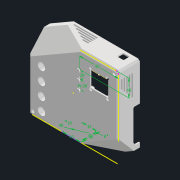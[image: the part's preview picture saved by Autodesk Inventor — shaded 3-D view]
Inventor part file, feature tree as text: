
AUTODESK INVENTOR PART (.ipt)
format: ipt  version: 2022 (Build 260153000, 153)  size: 850,944 bytes
history: native  units: mm
features: extrude x14, sketch x12, projected_geometry x9, fillet x8, other x8, chamfer x6, hole x5, reference x5, shell x1
ambient origin geometry x8: Origin, YZ Plane, XZ Plane, XY Plane, X Axis, Y Axis, Z Axis, Center Point
bodies: Solid1 (feature_tree)
feature tree (68):
  extrude  "Extrusion1"  Depth=2.0mm TaperAngle=45.0deg
  chamfer  "Chamfer1"  Distance=2.0mm Angle=45.0deg
  chamfer  "Chamfer2"  Distance=2.0mm Angle=45.0deg
  chamfer  "Chamfer3"  Distance=3.0mm
  shell  "Shell1"  Thickness=1.0mm
  extrude  "Extrusion2"  Depth=10.0mm
  hole  "Hole2"  [1 undecoded]
  chamfer  "Chamfer4"  Distance=30.0mm
  extrude  "Extrusion3"  Depth=30.0mm
  extrude  "Extrusion4"  Depth=3.0mm
  hole  "Hole3"  [1 undecoded]
  hole  "Hole4"  [1 undecoded]
  sketch  "Sketch12"  dims[d19=8.0mm d20=3.0mm d21=0.0mm]
  extrude  "Extrusion6"  Depth=5.0mm
  extrude  "Extrusion5"  Depth=5.0mm
  extrude  "Extrusion7"  Depth=5.0mm
  chamfer  "Chamfer6"  Distance=7.0mm
  fillet  "Fillet2"  [1 undecoded]
  fillet  "Fillet4"  Radius=3.0mm
  fillet  "Fillet5"  Radius=6.0mm
  fillet  "Fillet7"  Radius=7.0mm
  fillet  "Fillet8"  [1 undecoded]
  extrude  "Extrusion8"  Depth=3.0mm
  extrude  "top intake"  Depth=3.0mm
  extrude  "relay_out"  Depth=3.0mm
  chamfer  "Chamfer7"  Distance=3.0mm
  other  "fan_mount"
  extrude  "fan hole"  Depth=3.0mm
  extrude  "Extrusion14"  Depth=3.0mm TaperAngle=0.0deg
  fillet  "Fillet11"  Radius=2.0mm
  fillet  "Fillet12"  Radius=4.0mm
  hole  "Hole6"  [1 undecoded]
  extrude  "Extrusion15"  Depth=2.0mm
  extrude  "Extrusion12"  Depth=3.0mm
  fillet  "Fillet9"  Radius=20.0mm
  other  "led"
  hole  "Hole7"  [1 undecoded]
  sketch  "Sketch1"  dims[d0=50.0mm d1=0.0mm d2=36.0mm d3=2.0mm d4=45.0deg d5=36.0mm d6=2.0mm d7=45.0deg d8=4.0mm d9=2.0mm d10=45.0deg]
  reference  "Reference1"
  sketch  "Sketch2"  dims[d12=39.0mm]
  sketch  "Sketch4"  dims[d13=42.0mm]
  projected_geometry  "Projected Loop3"
  projected_geometry  "Projected Loop4"
  projected_geometry  "Projected Loop5"
  projected_geometry  "Projected Loop6"
  sketch  "Sketch6"  dims[d14=20.0mm]
  reference  "Reference2"
  sketch  "Sketch7"  dims[d15=20.0mm]
  reference  "Reference3"
  reference  "Reference4"
  sketch  "Sketch8"  dims[d17=8.0mm]
  sketch  "Sketch9"  dims[d18=8.0mm]
  projected_geometry  "Projected Loop9"
  projected_geometry  "Projected Loop10"
  projected_geometry  "Projected Loop11"
  sketch  "Sketch13"  dims[d29=3.6mm d30=6.0mm d31=6.5mm d32=3.4mm d33=90.0deg d34=8.0mm d35=20.594885mm]
  projected_geometry  "Projected Loop12"
  other  "air_intake"
  sketch  "Sketch17"  dims[d36=2.0mm d37=2.0mm d38=45.0deg d39=1.0mm]
  projected_geometry  "Projected Loop13"
  sketch  "Sketch18"  dims[d40=0.0mm d41=0.0mm d42=10.0mm]
  reference  "Reference5"
  sketch  "Sketch20"  dims[d43=10.0mm d44=40.0mm d45=0.0mm d48=3.6mm d49=6.0mm d50=6.8mm d51=30.0mm d52=90.0deg d53=8.0mm d54=20.594885mm d56=30.0mm d57=30.0mm d58=20.0mm d59=30.0mm d60=17.0mm d61=6.0mm d62=26.0mm d63=17.5mm d64=90.0deg d65=8.0mm d66=20.594885mm d71=5.0mm d72=5.0mm d73=5.0mm d74=5.0mm d75=7.0mm d76=0.0mm d82=3.0mm d84=6.0mm d89=7.0mm d90=0.0mm d92=3.0mm d93=3.0mm d94=3.0mm d95=3.0mm d96=22.0mm d97=15.0mm d98=0.0mm d99=8.0mm d100=2.0mm d101=45.0deg d102=4.0mm d104=2.0mm d105=2.0mm d107=1.0mm d108=20.0mm d109=10.0mm d110=20.0mm d111=20.0mm d112=10.0mm d113=10.0mm d115=0.0mm d116=0.0mm d117=2.0mm d118=32.0mm d119=32.0mm d120=3.0mm d121=3.0mm d122=5.0mm d123=3.0mm d124=10.0mm d125=5.0mm d126=5.0mm d127=3.0mm d128=50.0mm d129=0.0mm d130=15.0mm d131=10.0mm d132=10.0mm d133=78.0mm d134=10.0mm d135=0.0mm d136=2.0mm d137=2.0mm d138=45.0deg d139=8.0mm d141=40.0mm d142=40.0mm d143=10.0mm d144=0.0mm d152=2.0mm d153=10.0mm d154=0.0mm d155=40.0mm d156=2.0mm d157=15.4mm d162=4.0mm d163=0.0mm d164=3.0mm d165=3.0mm d166=3.4mm d167=6.0mm d168=6.5mm d169=3.4mm d170=14.3117mm d171=8.0mm d172=20.594885mm d187=4.0mm d188=0.0mm d190=20.0mm d191=3.0mm d192=3.0mm d193=3.0mm d194=3.0mm d195=3.0mm d196=3.0mm d197=3.0mm d198=3.0mm d199=3.0mm d201=20.0mm d202=20.0mm d203=52.0mm d208=5.3mm d209=6.0mm d210=6.5mm d211=3.4mm d212=14.3117mm d213=8.0mm d214=20.594885mm d216=20.0mm d217=20.0mm d218=40.0mm d260=90.0mm d261=18.0mm d262=3.0mm d263=5.0mm d80=3.0mm d81=0.0mm d83=0.0mm d264=0.5mm d265=0.872665mm]
  parser-record x1  (decoder bookkeeping rows leaked as tree rows — omitted from the tree; the rows remain in map.json)
  other  "Ensamble.iam"
  other  "base:1"
  other  "Nokia LCD:1"
  other  "Ardi_UNO:1"
note: 7 required parameter values undecoded (feature->parameter linkage not recoverable at this tier; creation-order binding heuristic only, values carry confidence <= 0.55)
note: 1 file-system path scrubbed to <path> (originals preserved in map.json)
